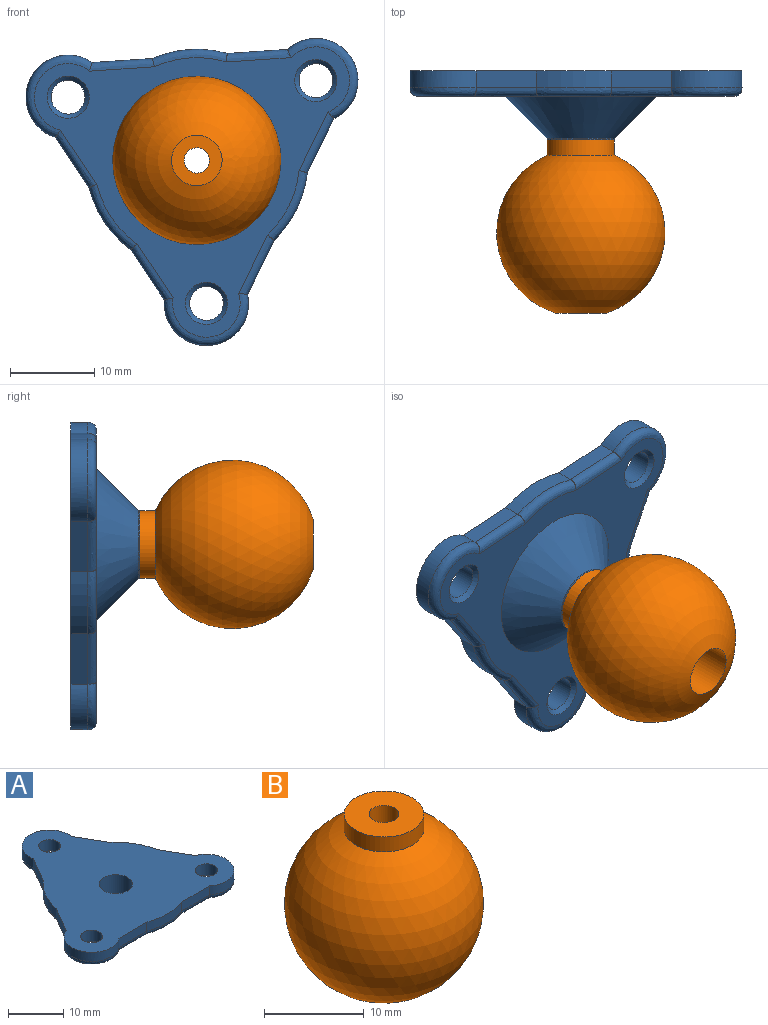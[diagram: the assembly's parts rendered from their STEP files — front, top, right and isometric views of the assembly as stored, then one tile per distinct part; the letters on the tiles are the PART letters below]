
ASSEMBLY  parts=2 mates=1
PART A: 38 faces, bbox 39.9x35.9x8.2 mm
  f0: plane 39.45x35.5mm, normal (0,0,1), area 761.5mm2, adj f4,f5,f6,f7,f8,f9,f10,f11
  f1: plane 37.53x33.55mm, normal (0,0,-1), area 395.3mm2, adj f3,f19,f20,f21,f22,f23,f24,f25
  f2: cylinder r=4mm len=8mm, axis (0,0,1), area 4.2mm2, adj f3,f31
  f3: cone r=9mm half-angle=45deg, axis (0,0,1), area 288.8mm2, adj f1,f2
  f4: cylinder r=2mm len=4mm, axis (0,0,-1), area 31.4mm2, adj f0,f35
  f5: cylinder r=2mm len=4mm, axis (0,0,-1), area 31.4mm2, adj f0,f37
  f6: cylinder r=2mm len=4mm, axis (0,0,-1), area 31.4mm2, adj f0,f36
  f7: plane 6.21x3.58mm, normal (0.87,0.5,0), area 14.3mm2, adj f0,f8,f11,f24
  f8: cylinder r=13.19mm len=7.7mm, axis (0,0,-1), area 18.1mm2, adj f0,f7,f9,f22
  f9: plane 6.21x3.58mm, normal (0.87,0.5,0), area 14.3mm2, adj f0,f8,f10,f20
  f10: cylinder r=5mm len=9.65mm, axis (0,0,-1), area 34.4mm2, adj f0,f9,f18,f19
  f11: cylinder r=5mm len=10mm, axis (0,0,-1), area 34.4mm2, adj f0,f7,f13,f26
  f12: cylinder r=13.19mm len=7.7mm, axis (0,0,-1), area 18.1mm2, adj f0,f13,f15,f30
  f13: plane 6.21x3.58mm, normal (-0.87,0.5,0), area 14.3mm2, adj f0,f11,f12,f28
  f14: cylinder r=5mm len=9.65mm, axis (0,0,-1), area 34.4mm2, adj f0,f15,f17,f27
  f15: plane 6.21x3.58mm, normal (-0.87,0.5,0), area 14.3mm2, adj f0,f12,f14,f29
  f16: cylinder r=13.19mm len=8.89mm, axis (0,0,-1), area 18.1mm2, adj f0,f17,f18,f23
  f17: plane 7.17x2mm, normal (0,-1,0), area 14.3mm2, adj f0,f14,f16,f25
  f18: plane 7.17x2mm, normal (0,-1,0), area 14.3mm2, adj f0,f10,f16,f21
  f19: bspline ~10.18x9.14mm, area 26.6mm2, adj f1,f10,f20,f21
  f20: bspline ~7.7x5.02mm, area 12.1mm2, adj f1,f9,f19,f22
  f21: bspline ~8.31x1mm, area 12.1mm2, adj f1,f18,f19,f23
  f22: bspline ~8.73x5.58mm, area 14.7mm2, adj f1,f8,f20,f24
  f23: bspline ~9.92x1.93mm, area 14.7mm2, adj f1,f16,f21,f25
  f24: bspline ~7.7x5.02mm, area 12.1mm2, adj f1,f7,f22,f26
  f25: bspline ~8.31x1mm, area 12.1mm2, adj f1,f17,f23,f27
  f26: bspline ~10.23x6.98mm, area 26.6mm2, adj f1,f11,f24,f28
  f27: bspline ~10.18x9.14mm, area 26.6mm2, adj f1,f14,f25,f29
  f28: bspline ~7.7x5.02mm, area 12.1mm2, adj f1,f13,f26,f30
  f29: bspline ~7.7x5.02mm, area 12.1mm2, adj f1,f15,f27,f30
  f30: bspline ~8.73x5.58mm, area 14.7mm2, adj f1,f12,f28,f29
  f31: plane 8x8mm, normal (0,0,-1), area 43.2mm2, adj f2,f34
  f32: cylinder r=3mm len=6mm, axis (0,0,1), area 84.8mm2, adj f0,f33
  f33: plane 6x6mm, normal (0,0,1), area 21.2mm2, adj f32,f34
  f34: cylinder r=1.5mm len=3.67mm, axis (0,0,1), area 34.5mm2, adj f31,f33
  f35: cone r=2.5mm half-angle=45deg, axis (0,0,-1), area 10mm2, adj f1,f4
  f36: cone r=2.5mm half-angle=45deg, axis (0,0,-1), area 10mm2, adj f1,f6
  f37: cone r=2.5mm half-angle=45deg, axis (0,0,-1), area 10mm2, adj f1,f5
PART B: 6 faces, bbox 20x20x20.5 mm
  f0: plane 8x8mm, normal (0,0,1), area 43.2mm2, adj f2,f3
  f1: sphere r=10mm, area 1175.2mm2, adj f2,f4
  f2: cylinder r=4mm len=8mm, axis (0,0,1), area 46.1mm2, adj f0,f1
  f3: cylinder r=1.5mm len=12mm, axis (0,0,1), area 113.1mm2, adj f0,f5
  f4: cylinder r=3mm len=8.54mm, axis (0,0,1), area 161mm2, adj f1,f5
  f5: plane 6x6mm, normal (0,0,-1), area 21.2mm2, adj f3,f4
PLACE A rot(axis=(-1,-0.03,-0.03),90.1deg) t=(0.02,-20,-0.07)mm fixed
PLACE B rot(axis=(-1,-0.03,-0.03),90.1deg) t=(0.02,-20,-0.07)mm
MATE fastened A.f34 <-> B.f3  axis (0,1,0) through (0.02,-9,-0.07)mm
